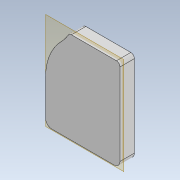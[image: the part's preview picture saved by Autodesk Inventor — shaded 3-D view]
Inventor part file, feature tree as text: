
AUTODESK INVENTOR PART (.ipt)
format: ipt  version: 2020.2 (Build 242310000, 310)  size: 208,896 bytes
history: native  units: in
note: dims shown in document units (in); Inventor stores cm internally (conversion verified against a paired STEP export)
features: extrude x6, sketch x6, other x3, thicken_offset x2, fillet x2, projected_geometry x2, plane x1
ambient origin geometry x8: Origin, YZ Plane, XZ Plane, XY Plane, X Axis, Y Axis, Z Axis, Center Point
bodies: Solid1 (feature_tree)
feature tree (22):
  plane  "Work Plane1"
  extrude  "Extrusion1"  Depth=0.063in
  thicken_offset  "Thicken1"
  extrude  "Extrusion2"  Depth=0.0394in
  fillet  "Fillet1"  Radius=0.0394in
  extrude  "Extrusion3"  Depth=0.1575in
  extrude  "Extrusion4"  Depth=0.0394in TaperAngle=0.0deg
  sketch  "Sketch6"  dims[d15=0.1476in d16=0.0394in d17=0.0in]
  extrude  "Extrusion5"  Depth=0.0394in TaperAngle=0.0deg
  extrude  "Extrusion6"  Depth=0.0394in
  fillet  "Fillet4"  Radius=0.0394in
  thicken_offset  "Thicken2"
  sketch  "Sketch2"  dims[d0=0.0098in d1=0.063in]
  sketch  "Sketch3"  dims[d2=0.5906in d3=0.0in d4=0.0394in d5=0.0394in]
  projected_geometry  "Projected Loop1"
  sketch  "Sketch4"  dims[d6=0.0472in d7=0.0in d8=0.1575in]
  projected_geometry  "Projected Loop2"
  sketch  "Sketch5"  dims[d11=0.1476in d12=0.0394in d13=0.0in]
  sketch  "Sketch7"  dims[d19=0.1476in d20=0.1476in d21=0.0394in d22=0.0in d23=0.0394in d24=0.0in d25=0.0394in d26=0.0394in d27=0.0394in]
  other  "<userpath>\Desktop\WemosLightSwitch\WemosLightSwitchV2.iam"
  other  "WemosLightSwitchV2.iam"
  other  "MainBaseV2:1"
